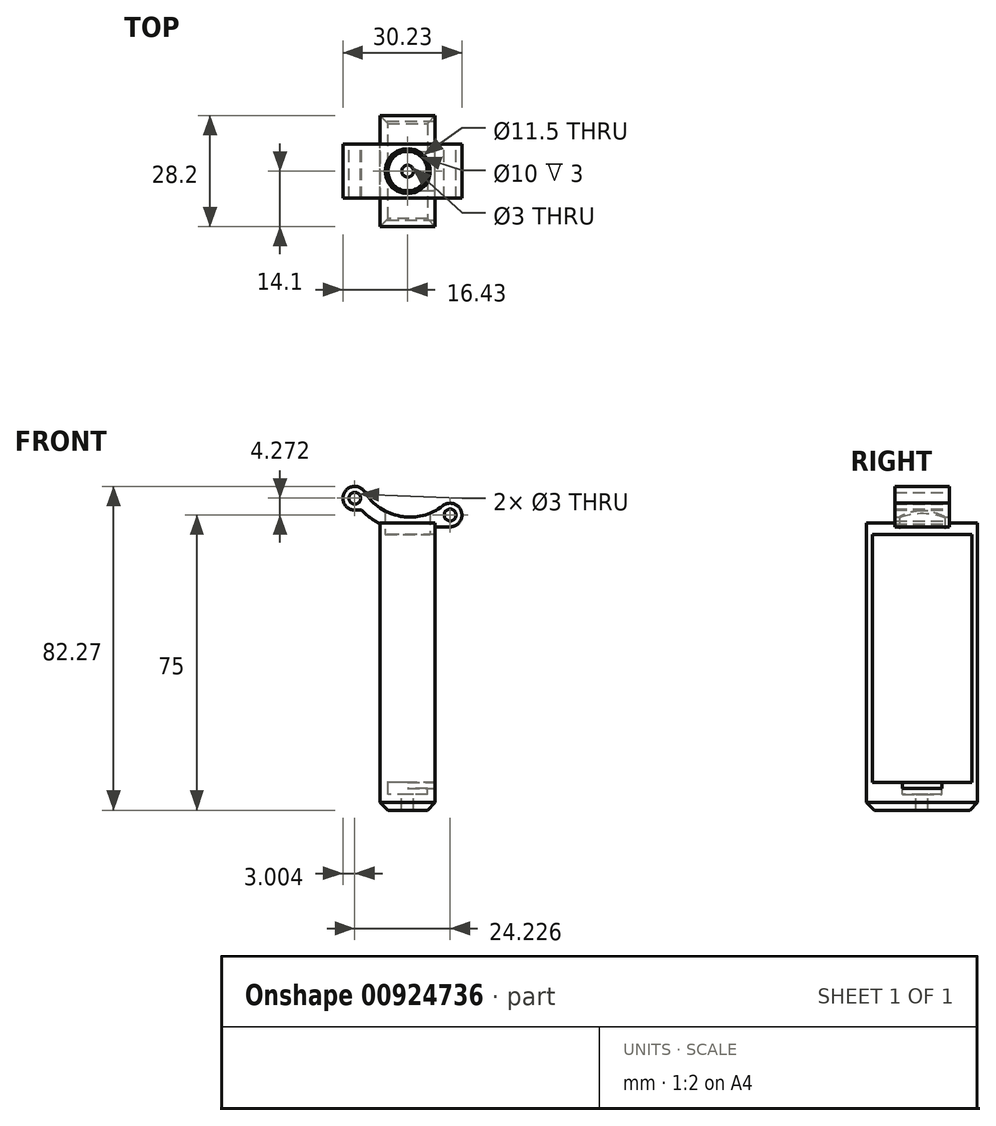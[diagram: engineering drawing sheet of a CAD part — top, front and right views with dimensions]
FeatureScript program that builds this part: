
annotation { "Feature Type Name" : "Feature", "Feature Type Description" : "" }
export const myFeature = defineFeature(function(context is Context, id is Id, definition is map)
    precondition{}
    {
        {
            var Q0;
            Q0=qCreatedBy(makeId("Front.planeOp"),FACE);
            var sketch = newSketch(context, id + "F0", { "sketchPlane" : qUnion([Q0])});
            skLineSegment(sketch, "E0", {"start": v(-7, 0) * mm, "end": v(7, 0) * mm});
            skLineSegment(sketch, "E1", {"start": v(7, 0) * mm, "end": v(7, 2) * mm});
            skLineSegment(sketch, "E2", {"start": v(7, 2) * mm, "end": v(10.8, 2) * mm});
            skLineSegment(sketch, "E3", {"start": v(10.8, 5) * mm, "end": v(-13.43, 9.27) * mm, "construction": true});
            skLineSegment(sketch, "E4", {"start": v(-13.43, 6.27) * mm, "end": v(-11.74, 6.27) * mm});
            skLineSegment(sketch, "E5", {"start": v(-7, 2.76) * mm, "end": v(-7, 0) * mm});
            skCircle(sketch, "E6", {"center": v(-13.43, 9.27) * mm, "radius": 1.5 * mm});
            skCircle(sketch, "E7", {"center": v(10.8, 5) * mm, "radius": 1.5 * mm});
            skArc(sketch, "E8", {"start": v(10.8, 2) * mm, "mid": v(13.63, 5.98) * mm, "end": v(8.94, 7.36) * mm});
            skArc(sketch, "E9", {"start": v(-10.88, 10.85) * mm, "mid": v(-16.05, 10.73) * mm, "end": v(-13.43, 6.27) * mm});
            skArc(sketch, "E10", {"start": v(-10.88, 10.85) * mm, "mid": v(-1.75, 4.67) * mm, "end": v(8.94, 7.36) * mm});
            skArc(sketch, "E11", {"start": v(-11.74, 6.27) * mm, "mid": v(-9.52, 4.3) * mm, "end": v(-7, 2.76) * mm});
            skSolve(sketch);
        }
        {
            var Q0;
            Q0=makeQuery(id+"F0.imprint","IMPRINT",FACE,{"disambiguationData":[TD([[makeQuery(id+"F0.imprint","IMPRINT",EDGE,{"derivedFrom":sQuery(id+"F0.wireOp",EDGE,"E0")}),1.0]])]});
            extrude(context, id + "F1", {"entities" : qUnion([Q0]), "depth" : 13.8 * mm, "offsetDistance" : 25 * mm, "symmetric" : true});
        }
        {
            var Q0;
            Q0=qCreatedBy(makeId("Right.planeOp"),FACE);
            var sketch = newSketch(context, id + "F2", { "sketchPlane" : qUnion([Q0])});
            skLineSegment(sketch, "E12.bottom", {"start": v(-14.1, 3) * mm, "end": v(14.1, 3) * mm});
            skLineSegment(sketch, "E12.top", {"start": v(-14.1, -70) * mm, "end": v(14.1, -70) * mm});
            skLineSegment(sketch, "E12.left", {"start": v(-14.1, 3) * mm, "end": v(-14.1, -70) * mm});
            skLineSegment(sketch, "E12.right", {"start": v(14.1, 3) * mm, "end": v(14.1, -70) * mm});
            skLineSegment(sketch, "E13.bottom", {"start": v(-12.6, 0) * mm, "end": v(12.6, 0) * mm});
            skLineSegment(sketch, "E13.top", {"start": v(-12.6, -63) * mm, "end": v(12.6, -63) * mm});
            skLineSegment(sketch, "E13.left", {"start": v(-12.6, 0) * mm, "end": v(-12.6, -63) * mm});
            skLineSegment(sketch, "E13.right", {"start": v(12.6, 0) * mm, "end": v(12.6, -63) * mm});
            skLineSegment(sketch, "E14", {"start": v(0, 0) * mm, "end": v(0, -63) * mm, "construction": true});
            skSolve(sketch);
        }
        {
            var Q0;
            Q0 = qSketchRegion(id + "F2", true);
            extrude(context, id + "F3", {"entities" : qUnion([Q0]), "operationType" : NewBodyOperationType.ADD, "depth" : 14 * mm, "offsetDistance" : 25 * mm, "symmetric" : true});
        }
        {
            var Q0;
            Q0=makeQuery(id+"F3.boolean.opBoolean","MERGE",FACE,{"derivedFrom":[makeQuery(id+"F1.opExtrude","SWEPT_FACE",FACE,{"disambiguationData":[OSD([sQuery(id+"F0.wireOp",EDGE,"E0")])]}),makeQuery(id+"F3.opExtrude","SWEPT_FACE",FACE,{"disambiguationData":[OSD([sQuery(id+"F2.wireOp",EDGE,"E13.bottom")])]})]});
            var sketch = newSketch(context, id + "F4", { "sketchPlane" : qUnion([Q0])});
            skCircle(sketch, "E15", {"center": v(0, 0) * mm, "radius": 5.75 * mm});
            skSolve(sketch);
        }
        {
            var Q0;
            Q0 = qSketchRegion(id + "F4", true);
            extrude(context, id + "F5", {"entities" : qUnion([Q0]), "operationType" : NewBodyOperationType.REMOVE, "endBound" : BoundingType.THROUGH_ALL, "oppositeDirection" : true, "depth" : 25 * mm, "offsetDistance" : 25 * mm});
        }
        {
            var Q0;
            Q0=makeQuery(id+"F3.opExtrude","SWEPT_FACE",FACE,{"disambiguationData":[OSD([sQuery(id+"F2.wireOp",EDGE,"E12.top")])]});
            chamfer(context, id + "F6", {"entities" : qUnion([Q0]), "width" : 2 * mm, "tangentPropagation" : true});
        }
        {
            var Q0;
            Q0=makeQuery(id+"F3.opExtrude","SWEPT_FACE",FACE,{"disambiguationData":[OSD([sQuery(id+"F2.wireOp",EDGE,"E13.top")])]});
            var sketch = newSketch(context, id + "F7", { "sketchPlane" : qUnion([Q0])});
            skCircle(sketch, "E16", {"center": v(0, 0) * mm, "radius": 1.5 * mm});
            skCircle(sketch, "E17", {"center": v(0, 0) * mm, "radius": 5 * mm});
            skLineSegment(sketch, "E18", {"start": v(0, 5) * mm, "end": v(7, 5) * mm});
            skLineSegment(sketch, "E19", {"start": v(0, -5) * mm, "end": v(7, -5) * mm});
            skLineSegment(sketch, "E20", {"start": v(7, -5) * mm, "end": v(7, 5) * mm});
            skSolve(sketch);
        }
        {
            var Q0;
            Q0=makeQuery(id+"F7.imprint","IMPRINT",FACE,{"disambiguationData":[TD([[makeQuery(id+"F7.imprint","IMPRINT",EDGE,{"derivedFrom":sQuery(id+"F7.wireOp",EDGE,"E16")}),-1.0]])]});
            extrude(context, id + "F8", {"entities" : qUnion([Q0]), "operationType" : NewBodyOperationType.REMOVE, "oppositeDirection" : true, "depth" : 3 * mm, "offsetDistance" : 25 * mm});
        }
        {
            var Q0;
            Q0=makeQuery(id+"F8.boolean.opBoolean","SPLIT",FACE,{"disambiguationData":[TD([makeQuery(id+"F8.opExtrude","SWEPT_FACE",FACE,{"disambiguationData":[OSD([sQuery(id+"F7.wireOp",EDGE,"E16")])]})])],"derivedFrom":makeQuery(id+"F3.opExtrude","SWEPT_FACE",FACE,{"disambiguationData":[OSD([sQuery(id+"F2.wireOp",EDGE,"E13.top")])]})});
            extrude(context, id + "F9", {"entities" : qUnion([Q0]), "operationType" : NewBodyOperationType.REMOVE, "endBound" : BoundingType.THROUGH_ALL, "oppositeDirection" : true, "depth" : 25 * mm, "offsetDistance" : 25 * mm});
        }
        {
            var Q0;
            {var subQ0=sQuery(id+"F7.wireOp",EDGE,"E18");Q0=makeQuery(id+"F7.imprint","IMPRINT",FACE,{"disambiguationData":[TD([[makeQuery(id+"F7.imprint","IMPRINT",EDGE,{"derivedFrom":subQ0}),-1.0]])]});}
            extrude(context, id + "F10", {"entities" : qUnion([Q0]), "operationType" : NewBodyOperationType.REMOVE, "oppositeDirection" : true, "depth" : 1.5 * mm, "offsetDistance" : 25 * mm});
        }
    });
